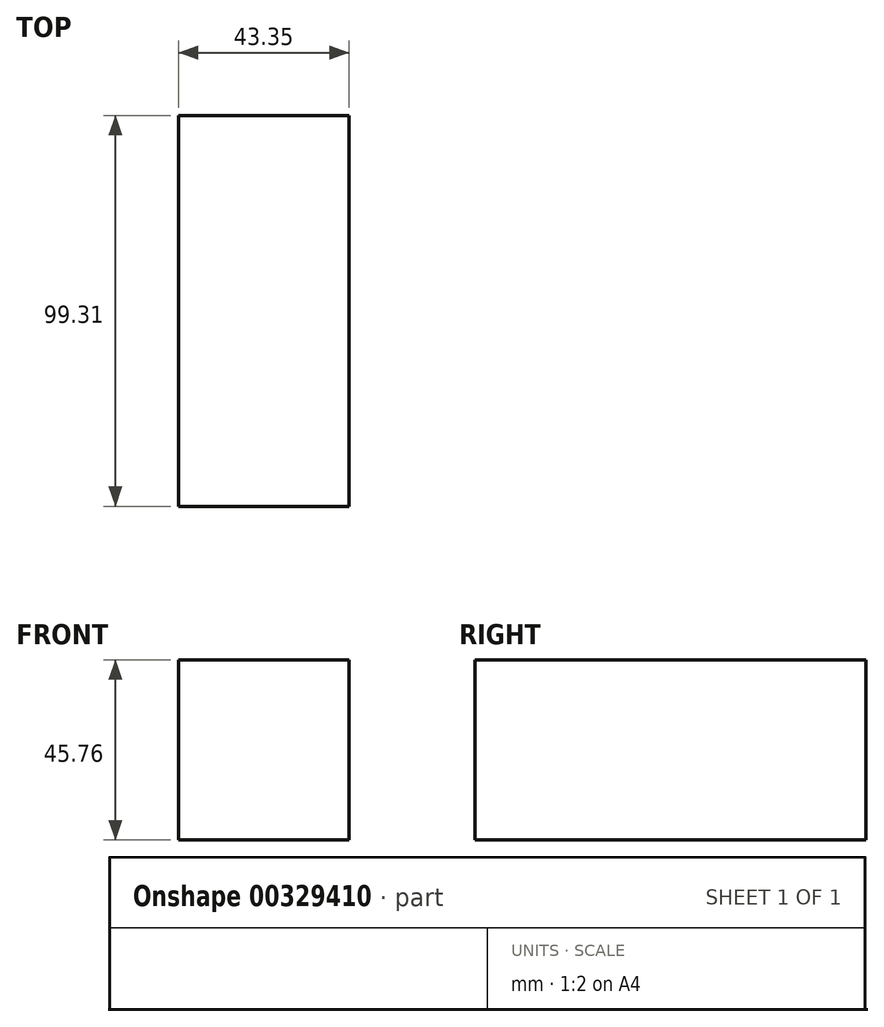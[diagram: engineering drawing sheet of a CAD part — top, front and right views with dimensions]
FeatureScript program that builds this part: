
annotation { "Feature Type Name" : "Feature", "Feature Type Description" : "" }
export const myFeature = defineFeature(function(context is Context, id is Id, definition is map)
    precondition{}
    {
        {
            var Q0;
            Q0=qCreatedBy(makeId("Front.planeOp"),FACE);
            var sketch = newSketch(context, id + "F0", { "sketchPlane" : qUnion([Q0])});
            skLineSegment(sketch, "E0.bottom", {"start": v(-26.87, 30.4) * mm, "end": v(-70.22, 30.4) * mm});
            skLineSegment(sketch, "E0.top", {"start": v(-26.87, 76.17) * mm, "end": v(-70.22, 76.17) * mm});
            skLineSegment(sketch, "E0.left", {"start": v(-26.87, 30.4) * mm, "end": v(-26.87, 76.17) * mm});
            skLineSegment(sketch, "E0.right", {"start": v(-70.22, 30.4) * mm, "end": v(-70.22, 76.17) * mm});
            skPoint(sketch, "E0.middle", {"position": v(-48.54, 53.3) * mm});
            skCircle(sketch, "E1", {"center": v(0, 0) * mm, "radius": 38.16 * mm});
            skArc(sketch, "E2", {"start": v(0, 0) * mm, "mid": v(35.57, 81.16) * mm, "end": v(-48.54, 53.3) * mm});
            skSolve(sketch);
        }
        {
            var Q0;
            Q0=makeQuery(id+"F0.imprint","IMPRINT",FACE,{"disambiguationData":[TD([[makeQuery(id+"F0.imprint","IMPRINT",EDGE,{"derivedFrom":sQuery(id+"F0.wireOp",EDGE,"E0.bottom")}),-1.0]])]});
            extrude(context, id + "F1", {"entities" : qUnion([Q0]), "depth" : 99.31 * mm});
        }
        {
            var Q0;
            Q0=makeQuery(id+"F1.opExtrude","SWEPT_FACE",FACE,{"disambiguationData":[OSD([sQuery(id+"F0.wireOp",EDGE,"E0.right")])]});
            var sketch = newSketch(context, id + "F2", { "sketchPlane" : qUnion([Q0])});
            skCircle(sketch, "E3", {"center": v(52.78, 57.79) * mm, "radius": 35.09 * mm});
            skSolve(sketch);
        }
        {
            var Q0;
            Q0=sQuery(id+"F2.wireOp",EDGE,"E3");
            extrude(context, id + "F3", {"bodyType" : ToolBodyType.SURFACE, "surfaceEntities" : qUnion([Q0]), "depth" : 41.4 * mm});
        }
    });
